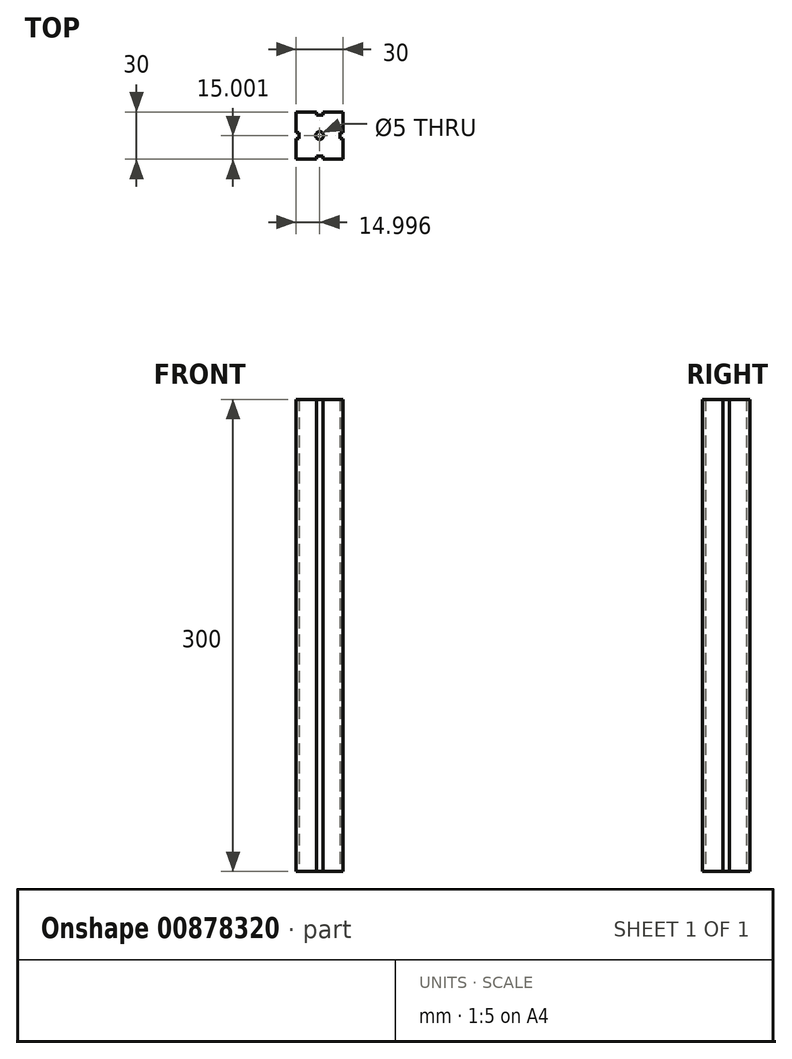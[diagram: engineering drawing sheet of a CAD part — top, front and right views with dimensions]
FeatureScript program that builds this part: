
annotation { "Feature Type Name" : "Feature", "Feature Type Description" : "" }
export const myFeature = defineFeature(function(context is Context, id is Id, definition is map)
    precondition{}
    {
        {
            var Q0;
            Q0=qCreatedBy(makeId("Top.planeOp"),FACE);
            var sketch = newSketch(context, id + "F0", { "sketchPlane" : qUnion([Q0])});
            skLineSegment(sketch, "E0.top", {"start": v(-52.64, -81.09) * mm, "end": v(-39.64, -81.09) * mm});
            skLineSegment(sketch, "E0.left", {"start": v(-52.64, -51.09) * mm, "end": v(-52.64, -64.09) * mm});
            skLineSegment(sketch, "E0.right", {"start": v(-22.64, -51.09) * mm, "end": v(-22.64, -64.09) * mm});
            skLineSegment(sketch, "E1", {"start": v(-52.64, -51.09) * mm, "end": v(-39.64, -51.09) * mm});
            skCircle(sketch, "E2", {"center": v(-37.64, -66.09) * mm, "radius": 2.5 * mm});
            skLineSegment(sketch, "E3.0", {"start": v(-39.64, -51.09) * mm, "end": v(-39.64, -53.09) * mm});
            skLineSegment(sketch, "E4.0", {"start": v(-39.64, -53.09) * mm, "end": v(-35.64, -53.09) * mm});
            skLineSegment(sketch, "E5.0", {"start": v(-35.64, -51.09) * mm, "end": v(-35.64, -53.09) * mm});
            skPoint(sketch, "E6.start.orphan", {"position": v(-37.64, -51.09) * mm});
            skLineSegment(sketch, "E7.MirrorCS", {"start": v(-35.64, -81.09) * mm, "end": v(-35.64, -79.09) * mm});
            skLineSegment(sketch, "E8.MirrorCS", {"start": v(-39.64, -81.09) * mm, "end": v(-39.64, -79.09) * mm});
            skLineSegment(sketch, "E9.MirrorCS", {"start": v(-39.64, -79.09) * mm, "end": v(-35.64, -79.09) * mm});
            skLineSegment(sketch, "E10.1.0", {"start": v(-50.64, -64.09) * mm, "end": v(-50.64, -68.09) * mm});
            skLineSegment(sketch, "E10.1.1", {"start": v(-52.64, -64.09) * mm, "end": v(-50.64, -64.09) * mm});
            skLineSegment(sketch, "E10.1.2", {"start": v(-52.64, -68.09) * mm, "end": v(-50.64, -68.09) * mm});
            skLineSegment(sketch, "E10.1.3", {"start": v(-22.64, -64.09) * mm, "end": v(-24.64, -64.09) * mm});
            skLineSegment(sketch, "E10.1.4", {"start": v(-24.64, -64.09) * mm, "end": v(-24.64, -68.09) * mm});
            skLineSegment(sketch, "E10.1.5", {"start": v(-22.64, -68.09) * mm, "end": v(-24.64, -68.09) * mm});
            skLineSegment(sketch, "E10.anchor1", {"start": v(-37.64, -66.09) * mm, "end": v(-39.64, -81.09) * mm, "construction": true});
            skLineSegment(sketch, "E10.anchor2", {"start": v(-37.64, -66.09) * mm, "end": v(-52.64, -64.09) * mm, "construction": true});
            skLineSegment(sketch, "E11.trimOffspring", {"start": v(-52.64, -68.09) * mm, "end": v(-52.64, -81.09) * mm});
            skLineSegment(sketch, "E12.trimOffspring", {"start": v(-35.64, -51.09) * mm, "end": v(-22.64, -51.09) * mm});
            skLineSegment(sketch, "E13.trimOffspring", {"start": v(-22.64, -68.09) * mm, "end": v(-22.64, -81.09) * mm});
            skLineSegment(sketch, "E14.trimOffspring", {"start": v(-35.64, -81.09) * mm, "end": v(-22.64, -81.09) * mm});
            skSolve(sketch);
        }
        {
            var Q0;
            Q0=makeQuery(id+"F0.imprint","IMPRINT",FACE,{"disambiguationData":[TD([[makeQuery(id+"F0.imprint","IMPRINT",EDGE,{"derivedFrom":sQuery(id+"F0.wireOp",EDGE,"E0.top")}),1.0]])]});
            extrude(context, id + "F1", {"entities" : qUnion([Q0]), "depth" : 300 * mm, "offsetDistance" : 25 * mm});
        }
    });
